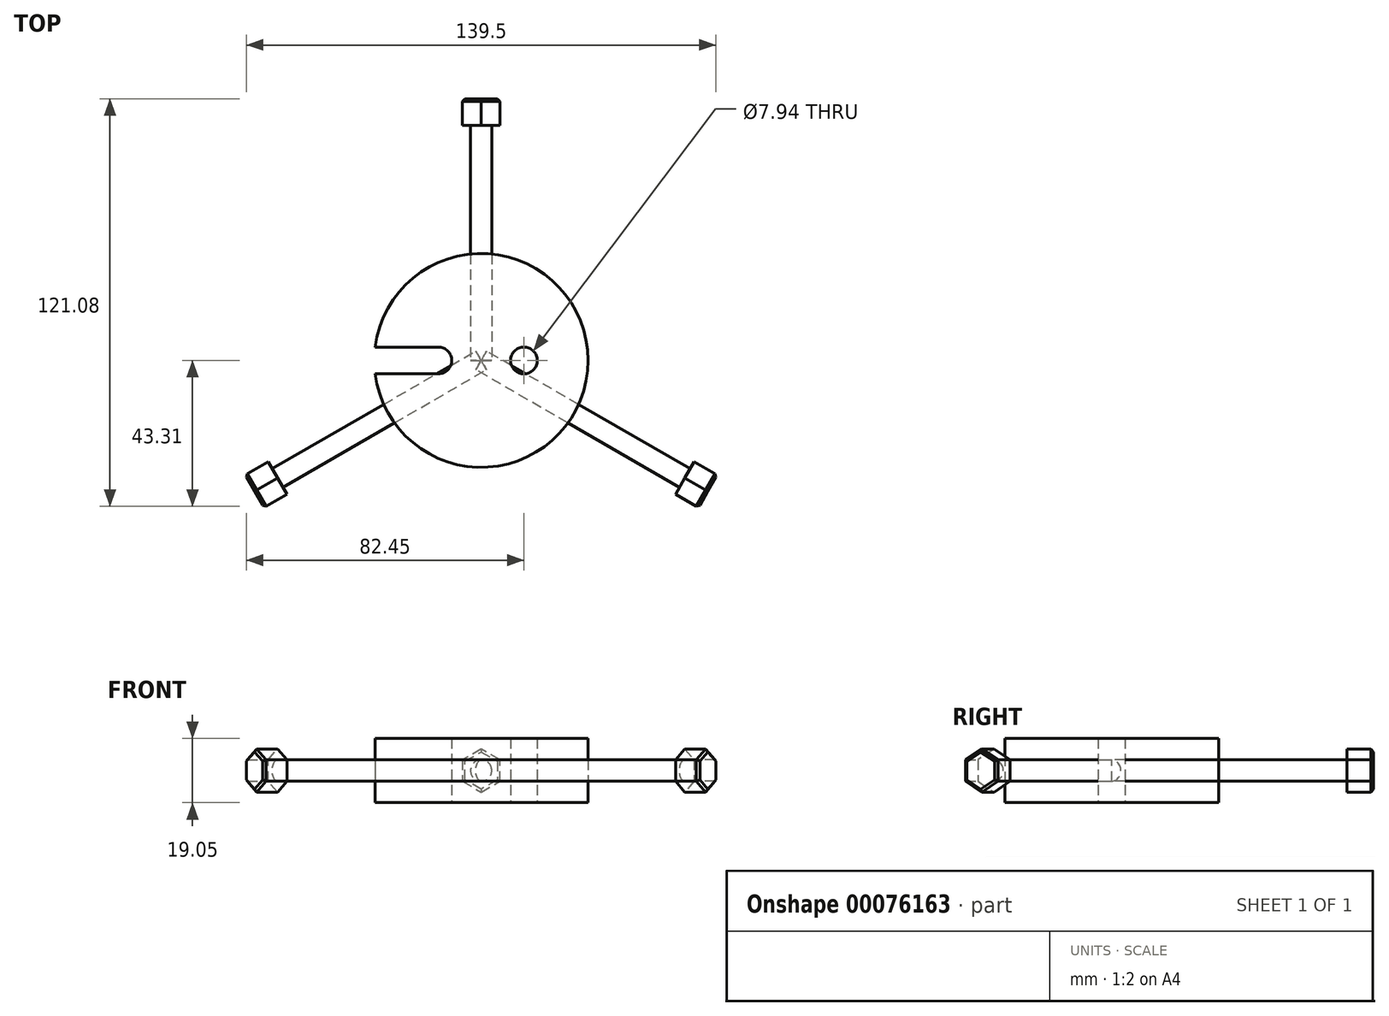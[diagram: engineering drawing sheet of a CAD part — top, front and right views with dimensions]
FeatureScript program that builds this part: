
annotation { "Feature Type Name" : "Feature", "Feature Type Description" : "" }
export const myFeature = defineFeature(function(context is Context, id is Id, definition is map)
    precondition{}
    {
        {
            var Q0;
            Q0=qCreatedBy(makeId("Top.planeOp"),FACE);
            var sketch = newSketch(context, id + "F0", { "sketchPlane" : qUnion([Q0])});
            skArc(sketch, "E0", {"start": v(-31.5, -3.96) * mm, "mid": v(31.75, 0) * mm, "end": v(-31.5, 3.96) * mm});
            skCircle(sketch, "E1", {"center": v(12.7, 0) * mm, "radius": 3.97 * mm});
            skArc(sketch, "E2", {"start": v(-12.7, -3.96) * mm, "mid": v(-8.74, 0) * mm, "end": v(-12.7, 3.96) * mm});
            skLineSegment(sketch, "E3", {"start": v(-12.7, 3.96) * mm, "end": v(-31.5, 3.96) * mm});
            skLineSegment(sketch, "E4", {"start": v(-12.7, -3.96) * mm, "end": v(-31.5, -3.96) * mm});
            skSolve(sketch);
        }
        {
            var Q0;
            Q0 = qSketchRegion(id + "F0", true);
            extrude(context, id + "F1", {"entities" : qUnion([Q0]), "depth" : 19.05 * mm, "offsetDistance" : 25.4 * mm});
        }
        {
            var Q0;
            Q0=qCreatedBy(makeId("Front.planeOp"),FACE);
            var sketch = newSketch(context, id + "F2", { "sketchPlane" : qUnion([Q0])});
            skCircle(sketch, "E5", {"center": v(0, 9.53) * mm, "radius": 3.17 * mm});
            skSolve(sketch);
        }
        {
            var Q0;
            Q0 = qSketchRegion(id + "F2", true);
            extrude(context, id + "F3", {"entities" : qUnion([Q0]), "oppositeDirection" : true, "depth" : 69.85 * mm, "offsetDistance" : 25.4 * mm});
        }
        {
            var Q0;
            Q0=makeQuery(id+"F3.opExtrude","CAP_FACE",FACE,{"disambiguationData":[OSD([sQuery(id+"F2.wireOp",EDGE,"E5")])],"isStart":false});
            var sketch = newSketch(context, id + "F4", { "sketchPlane" : qUnion([Q0])});
            skCircle(sketch, "E6.cCircle", {"center": v(0, 9.53) * mm, "radius": 5.55 * mm, "construction": true});
            skLineSegment(sketch, "E6.0", {"start": v(5.55, 12.73) * mm, "end": v(5.55, 6.32) * mm});
            skLineSegment(sketch, "E6.1", {"start": v(5.55, 6.32) * mm, "end": v(0, 3.12) * mm});
            skLineSegment(sketch, "E6.2", {"start": v(0, 3.12) * mm, "end": v(-5.55, 6.32) * mm});
            skLineSegment(sketch, "E6.3", {"start": v(-5.55, 6.32) * mm, "end": v(-5.55, 12.73) * mm});
            skLineSegment(sketch, "E6.4", {"start": v(-5.55, 12.73) * mm, "end": v(0, 15.93) * mm});
            skLineSegment(sketch, "E6.5", {"start": v(0, 15.93) * mm, "end": v(5.55, 12.73) * mm});
            skPoint(sketch, "E6.0.midPoint", {"position": v(5.55, 9.53) * mm});
            skSolve(sketch);
        }
        {
            var Q0;
            Q0 = qSketchRegion(id + "F4", true);
            extrude(context, id + "F5", {"entities" : qUnion([Q0]), "operationType" : NewBodyOperationType.ADD, "depth" : 7.92 * mm, "offsetDistance" : 25.4 * mm});
        }
        {
            var Q0;
            Q0=makeQuery(id+"F5.opExtrude","CAP_FACE",FACE,{"disambiguationData":[OSD([sQuery(id+"F4.wireOp",EDGE,"E6.0"),sQuery(id+"F4.wireOp",EDGE,"E6.1"),sQuery(id+"F4.wireOp",EDGE,"E6.2"),sQuery(id+"F4.wireOp",EDGE,"E6.3"),sQuery(id+"F4.wireOp",EDGE,"E6.4"),sQuery(id+"F4.wireOp",EDGE,"E6.5")])],"isStart":false});
            chamfer(context, id + "F6", {"entities" : qUnion([Q0]), "width" : 0.76 * mm, "tangentPropagation" : true});
        }
        {
            var Q0;
            Q0=makeQuery(id+"F3.opExtrude","SWEPT_BODY",BODY,{"disambiguationData":[OSD([sQuery(id+"F2.wireOp",EDGE,"E5")])]});
            var Q1;
            Q1=makeQuery(id+"F1.opExtrude","SWEPT_FACE",FACE,{"disambiguationData":[OSD([sQuery(id+"F0.wireOp",EDGE,"E0")])]});
            circularPattern(context, id + "F7", {"entities" : qUnion([Q0]), "axis" : qUnion([Q1]), "angle" : 360 * degree, "instanceCount" : 3, "equalSpace" : true});
        }
    });
